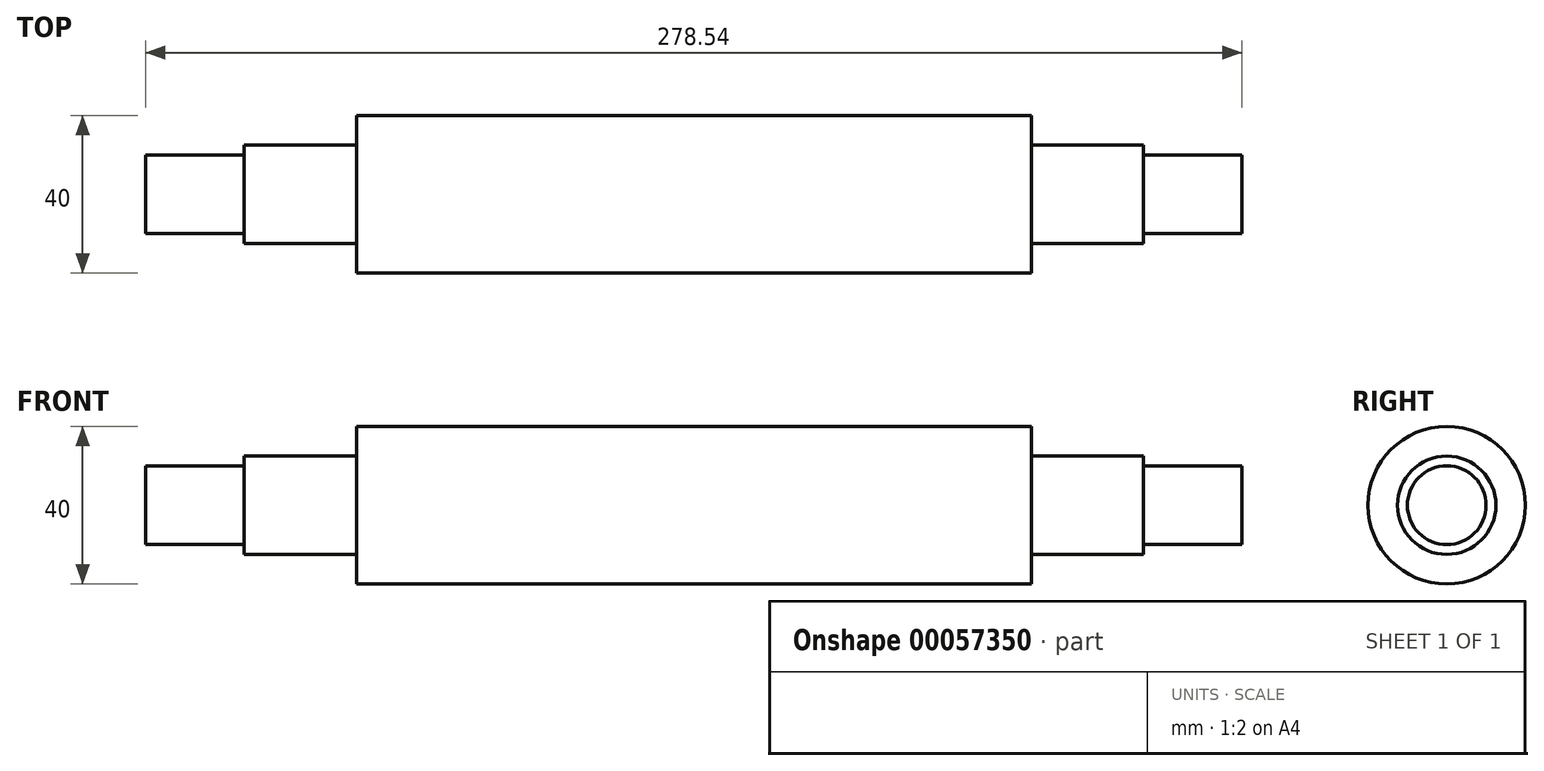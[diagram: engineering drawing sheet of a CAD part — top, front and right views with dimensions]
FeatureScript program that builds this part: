
annotation { "Feature Type Name" : "Feature", "Feature Type Description" : "" }
export const myFeature = defineFeature(function(context is Context, id is Id, definition is map)
    precondition{}
    {
        {
            var Q0;
            Q0=qCreatedBy(makeId("Right.planeOp"),FACE);
            var sketch = newSketch(context, id + "F0", { "sketchPlane" : qUnion([Q0])});
            skCircle(sketch, "E0", {"center": v(0, 0) * mm, "radius": 20 * mm});
            skSolve(sketch);
        }
        {
            var Q0;
            Q0 = qSketchRegion(id + "F0", true);
            extrude(context, id + "F1", {"entities" : qUnion([Q0]), "depth" : 171.5 * mm});
        }
        {
            var Q0;
            Q0=makeQuery(id+"F1.opExtrude","CAP_FACE",FACE,{"disambiguationData":[OSD([sQuery(id+"F0.wireOp",EDGE,"E0")])],"isStart":false});
            var sketch = newSketch(context, id + "F2", { "sketchPlane" : qUnion([Q0])});
            skCircle(sketch, "E1", {"center": v(0, 0) * mm, "radius": 12.5 * mm});
            skSolve(sketch);
        }
        {
            var Q0;
            Q0 = qSketchRegion(id + "F2", true);
            extrude(context, id + "F3", {"entities" : qUnion([Q0]), "operationType" : NewBodyOperationType.ADD, "depth" : 28.52 * mm});
        }
        {
            var Q0;
            Q0=makeQuery(id+"F1.opExtrude","CAP_FACE",FACE,{"disambiguationData":[OSD([sQuery(id+"F0.wireOp",EDGE,"E0")])],"isStart":true});
            var sketch = newSketch(context, id + "F4", { "sketchPlane" : qUnion([Q0])});
            skCircle(sketch, "E2", {"center": v(0, 0) * mm, "radius": 12.5 * mm});
            skSolve(sketch);
        }
        {
            var Q0;
            Q0 = qSketchRegion(id + "F4", true);
            extrude(context, id + "F5", {"entities" : qUnion([Q0]), "operationType" : NewBodyOperationType.ADD, "depth" : 28.52 * mm});
        }
        {
            var Q0;
            Q0=makeQuery(id+"F3.opExtrude","CAP_FACE",FACE,{"disambiguationData":[OSD([sQuery(id+"F2.wireOp",EDGE,"E1")])],"isStart":false});
            var sketch = newSketch(context, id + "F6", { "sketchPlane" : qUnion([Q0])});
            skCircle(sketch, "E3", {"center": v(0, 0) * mm, "radius": 10 * mm});
            skSolve(sketch);
        }
        {
            var Q0;
            Q0=makeQuery(id+"F6.imprint","IMPRINT",FACE,{"disambiguationData":[TD([[makeQuery(id+"F6.imprint","IMPRINT",EDGE,{"derivedFrom":sQuery(id+"F6.wireOp",EDGE,"E3")}),1.0]])]});
            extrude(context, id + "F7", {"entities" : qUnion([Q0]), "operationType" : NewBodyOperationType.ADD, "depth" : 25 * mm});
        }
        {
            var Q0;
            Q0=makeQuery(id+"F5.opExtrude","CAP_FACE",FACE,{"disambiguationData":[OSD([sQuery(id+"F4.wireOp",EDGE,"E2")])],"isStart":false});
            var sketch = newSketch(context, id + "F8", { "sketchPlane" : qUnion([Q0])});
            skCircle(sketch, "E4", {"center": v(0, 0) * mm, "radius": 10 * mm});
            skSolve(sketch);
        }
        {
            var Q0;
            Q0=makeQuery(id+"F8.imprint","IMPRINT",FACE,{"disambiguationData":[TD([[makeQuery(id+"F8.imprint","IMPRINT",EDGE,{"derivedFrom":sQuery(id+"F8.wireOp",EDGE,"E4")}),1.0]])]});
            extrude(context, id + "F9", {"entities" : qUnion([Q0]), "operationType" : NewBodyOperationType.ADD, "depth" : 25 * mm});
        }
    });
